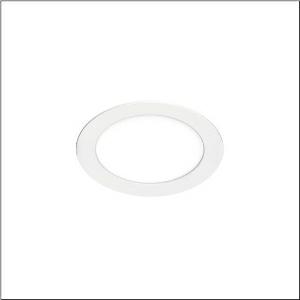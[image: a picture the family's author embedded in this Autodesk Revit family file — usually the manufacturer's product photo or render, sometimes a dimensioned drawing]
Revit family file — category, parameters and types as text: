
# Revit family: lunis_41_flat_51dr10dfgcb
name_source: partatom
category: Lighting Fixtures
units: mm (PartAtom-declared; Revit-internal decimal feet)

## family parameters
Cut with Voids When Loaded = No
Host = Face
Light Source = No
Part Type = Normal
Room Calculation Point = No
Round Connector Dimension = Use Diameter
Shared = No

## types (1)
- --- (1 x LED, 1550 lm, 11.5 W, 4000K)
    Apparent Load = 12 VA
    CIE Flux Codes = 49 80 96 100 100
    Color Rendering = 80
    Color Temperature = 4000K
    Default Elevation = 1800 mm
    Description = Lunis 41,  Flat, downlight, light emission: direct distribution, LED rated luminous flux: 2.450lm, light colour: 830/840, control gear: ECG, mains connection: 230V, AC, 50/60Hz, housing, round, of aluminium, coated, traffic white (RAL 9016), diameter: 225mm, protection rating (complete): IP20, protection rating (on room side): IP44, insulation class (complete): insulation class II (safety insulation), certification: CE, permissible ambient temperature for indoor applications: -20..+40°C, packaging unit: 1 piece
    Height = 0 mm  [stored 0 ft]
    Lamp = 1 x LED
    Lamp Light Flux = 1550 lm
    Lamp Power = 11.5 W
    Lamp count = 1
    Length = 225 mm
    Luminous efficacy = 135 lm/W
    Manufacturer = Siteco
    ModVariant = No
    Model = 51DR10DFGCB
    Mounting Place = Ceiling
    Mounting Type = Recessed
    Number of Poles = 1
    OnlyDefault = Yes
    Power Factor = 1
    Product Name = Lunis 41 Flat
    Product group = downlight
    ProductGroupID = 401
    Protection Class = Protection class II
    Protection Degree = IP 20
    RLX_Detail_Level = 1
    RLX_Emergency_Light_Flux = 0 lm
    RLX_Emergency_Type = 0
    RLX_Emergency_Type_DB = No
    RlxData = <blob elided: 13829 chars, md5=63cc7e9b>
    Socket = socket
    Standby Power = 0 W
    System Light Flux = 1550 lm
    System Power = 12 W
    Type Comments = factory setting: colour temperature 4000K, luminous flux: 50 % | (ON | ON | ON) | 350 mA
    Type Image = l_1340923.jpg
    URL = http://relux.com
    VarID = @adj_018887
    Voltage = 0 V
    Weight = 0.00 kg
    Width = 0 mm  [stored 0 ft]

note: [stored X ft] marks values corroborated as IEEE doubles in the binary element streams (Revit-internal decimal feet)

## geometry (parser evidence)
native form markers: Sweep x11
no freeform markers — native parametric forms only
